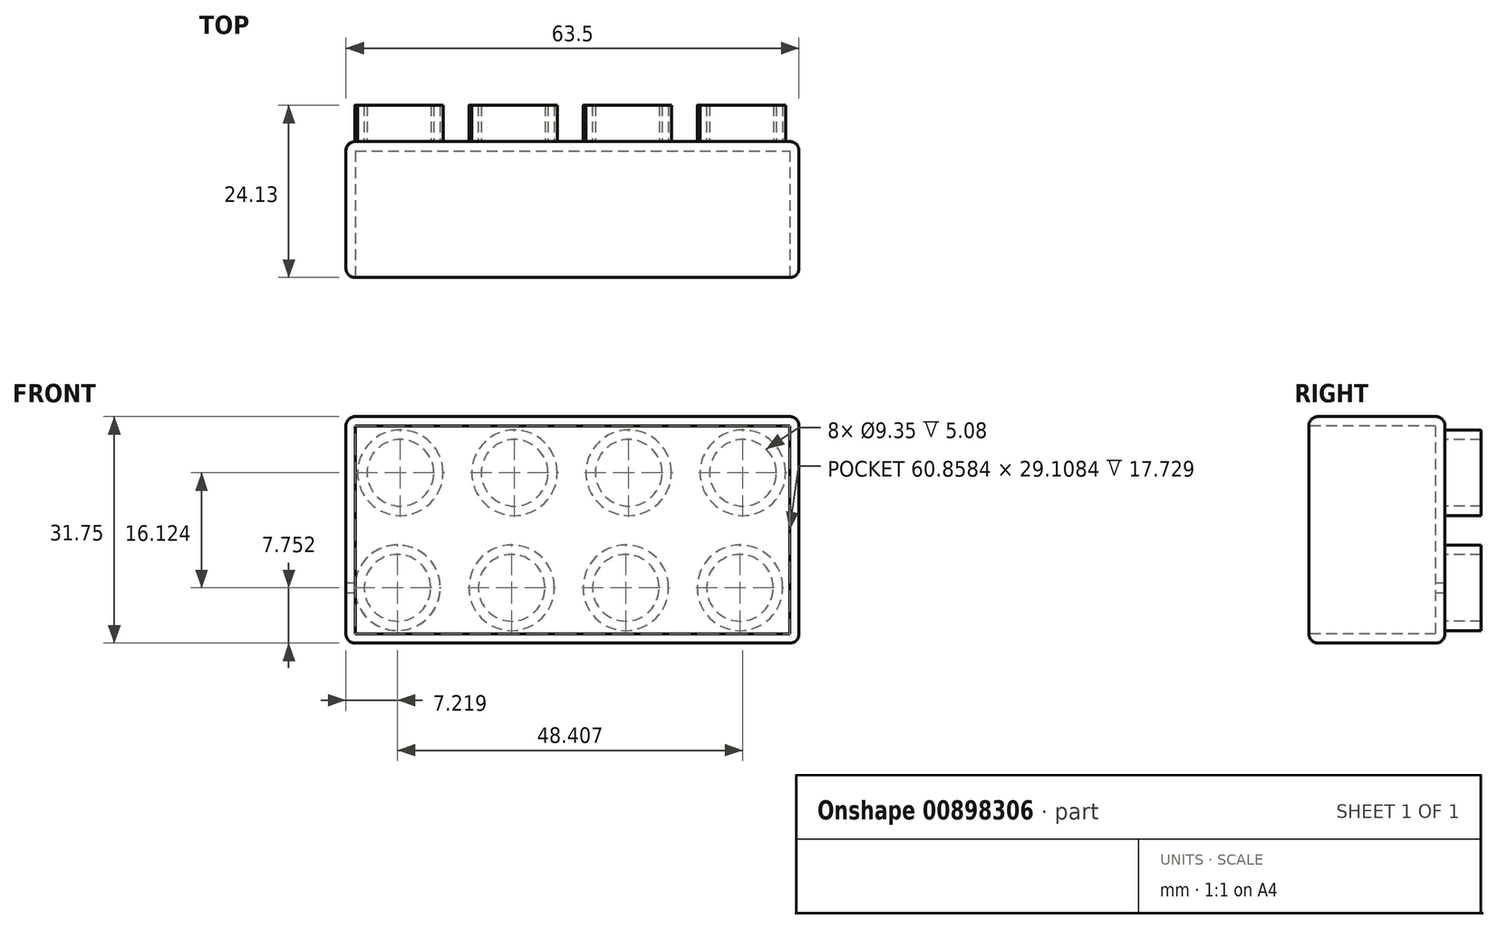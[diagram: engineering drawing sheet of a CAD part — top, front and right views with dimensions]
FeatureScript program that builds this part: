
annotation { "Feature Type Name" : "Feature", "Feature Type Description" : "" }
export const myFeature = defineFeature(function(context is Context, id is Id, definition is map)
    precondition{}
    {
        {
            var Q0;
            Q0=qCreatedBy(makeId("Top.planeOp"),FACE);
            var sketch = newSketch(context, id + "F0", { "sketchPlane" : qUnion([Q0])});
            skLineSegment(sketch, "E0.bottom", {"start": v(-63.5, 19.05) * mm, "end": v(0, 19.05) * mm});
            skLineSegment(sketch, "E0.top", {"start": v(-63.5, 0) * mm, "end": v(0, 0) * mm});
            skLineSegment(sketch, "E0.left", {"start": v(-63.5, 19.05) * mm, "end": v(-63.5, 0) * mm});
            skLineSegment(sketch, "E0.right", {"start": v(0, 19.05) * mm, "end": v(0, 0) * mm});
            skSolve(sketch);
        }
        {
            var Q0;
            Q0=makeQuery(id+"F0.imprint","IMPRINT",FACE,{"disambiguationData":[TD([[makeQuery(id+"F0.imprint","IMPRINT",EDGE,{"derivedFrom":sQuery(id+"F0.wireOp",EDGE,"E0.bottom")}),-1.0]])]});
            extrude(context, id + "F1", {"entities" : qUnion([Q0]), "depth" : 31.75 * mm, "offsetDistance" : 25.4 * mm});
        }
        {
            var Q0;
            Q0=makeQuery(id+"F1.opExtrude","SWEPT_FACE",FACE,{"disambiguationData":[OSD([sQuery(id+"F0.wireOp",EDGE,"E0.top")])]});
            shell(context, id + "F2", {"entities" : qUnion([Q0]), "thickness" : 1.32 * mm});
        }
        {
            var Q0;
            Q0=makeQuery(id+"F1.opExtrude","SWEPT_FACE",FACE,{"disambiguationData":[OSD([sQuery(id+"F0.wireOp",EDGE,"E0.bottom")])]});
            var sketch = newSketch(context, id + "F3", { "sketchPlane" : qUnion([Q0])});
            skCircle(sketch, "E1", {"center": v(7.87, 23.88) * mm, "radius": 4.67 * mm});
            skCircle(sketch, "E2.0", {"center": v(7.87, 23.88) * mm, "radius": 6 * mm});
            skCircle(sketch, "E3.1.0.0", {"center": v(23.88, 23.88) * mm, "radius": 4.67 * mm});
            skCircle(sketch, "E3.1.0.1", {"center": v(23.88, 23.88) * mm, "radius": 6 * mm});
            skCircle(sketch, "E3.2.0.0", {"center": v(39.88, 23.88) * mm, "radius": 4.67 * mm});
            skCircle(sketch, "E3.2.0.1", {"center": v(39.88, 23.88) * mm, "radius": 6 * mm});
            skCircle(sketch, "E3.3.0.0", {"center": v(55.88, 23.88) * mm, "radius": 4.67 * mm});
            skCircle(sketch, "E3.3.0.1", {"center": v(55.88, 23.88) * mm, "radius": 6 * mm});
            skCircle(sketch, "E4.1.0.0", {"center": v(24.28, 7.75) * mm, "radius": 4.67 * mm});
            skCircle(sketch, "E4.1.0.1", {"center": v(8.28, 7.75) * mm, "radius": 6 * mm});
            skCircle(sketch, "E4.1.0.2", {"center": v(56.28, 7.75) * mm, "radius": 4.67 * mm});
            skCircle(sketch, "E4.1.0.3", {"center": v(8.28, 7.75) * mm, "radius": 4.67 * mm});
            skCircle(sketch, "E4.1.0.4", {"center": v(56.28, 7.75) * mm, "radius": 6 * mm});
            skCircle(sketch, "E4.1.0.5", {"center": v(40.28, 7.75) * mm, "radius": 4.67 * mm});
            skCircle(sketch, "E4.1.0.6", {"center": v(40.28, 7.75) * mm, "radius": 6 * mm});
            skCircle(sketch, "E4.1.0.7", {"center": v(24.28, 7.75) * mm, "radius": 6 * mm});
            skLineSegment(sketch, "E4.direction1", {"start": v(7.87, 23.88) * mm, "end": v(8.28, 7.75) * mm, "construction": true});
            skSolve(sketch);
        }
        {
            var Q0;
            Q0 = qSketchRegion(id + "F3", true);
            extrude(context, id + "F4", {"entities" : qUnion([Q0]), "operationType" : NewBodyOperationType.ADD, "depth" : 5.08 * mm, "offsetDistance" : 25.4 * mm});
        }
        {
            var Q0;
            Q0=makeQuery(id+"F1.opExtrude","CAP_FACE",FACE,{"disambiguationData":[OSD([sQuery(id+"F0.wireOp",EDGE,"E0.bottom"),sQuery(id+"F0.wireOp",EDGE,"E0.top"),sQuery(id+"F0.wireOp",EDGE,"E0.left"),sQuery(id+"F0.wireOp",EDGE,"E0.right")])],"isStart":false});
            var Q1;
            Q1=makeQuery(id+"F1.opExtrude","SWEPT_FACE",FACE,{"disambiguationData":[OSD([sQuery(id+"F0.wireOp",EDGE,"E0.left")])]});
            var Q2;
            Q2=makeQuery(id+"F1.opExtrude","SWEPT_FACE",FACE,{"disambiguationData":[OSD([sQuery(id+"F0.wireOp",EDGE,"E0.right")])]});
            var Q3;
            Q3=makeQuery(id+"F1.opExtrude","CAP_FACE",FACE,{"disambiguationData":[OSD([sQuery(id+"F0.wireOp",EDGE,"E0.bottom"),sQuery(id+"F0.wireOp",EDGE,"E0.top"),sQuery(id+"F0.wireOp",EDGE,"E0.left"),sQuery(id+"F0.wireOp",EDGE,"E0.right")])],"isStart":true});
            fillet(context, id + "F5", {"entities" : qUnion([Q0, Q1, Q2, Q3]), "radius" : 1.27 * mm, "tangentPropagation" : true, "allowEdgeOverflow" : false});
        }
    });
